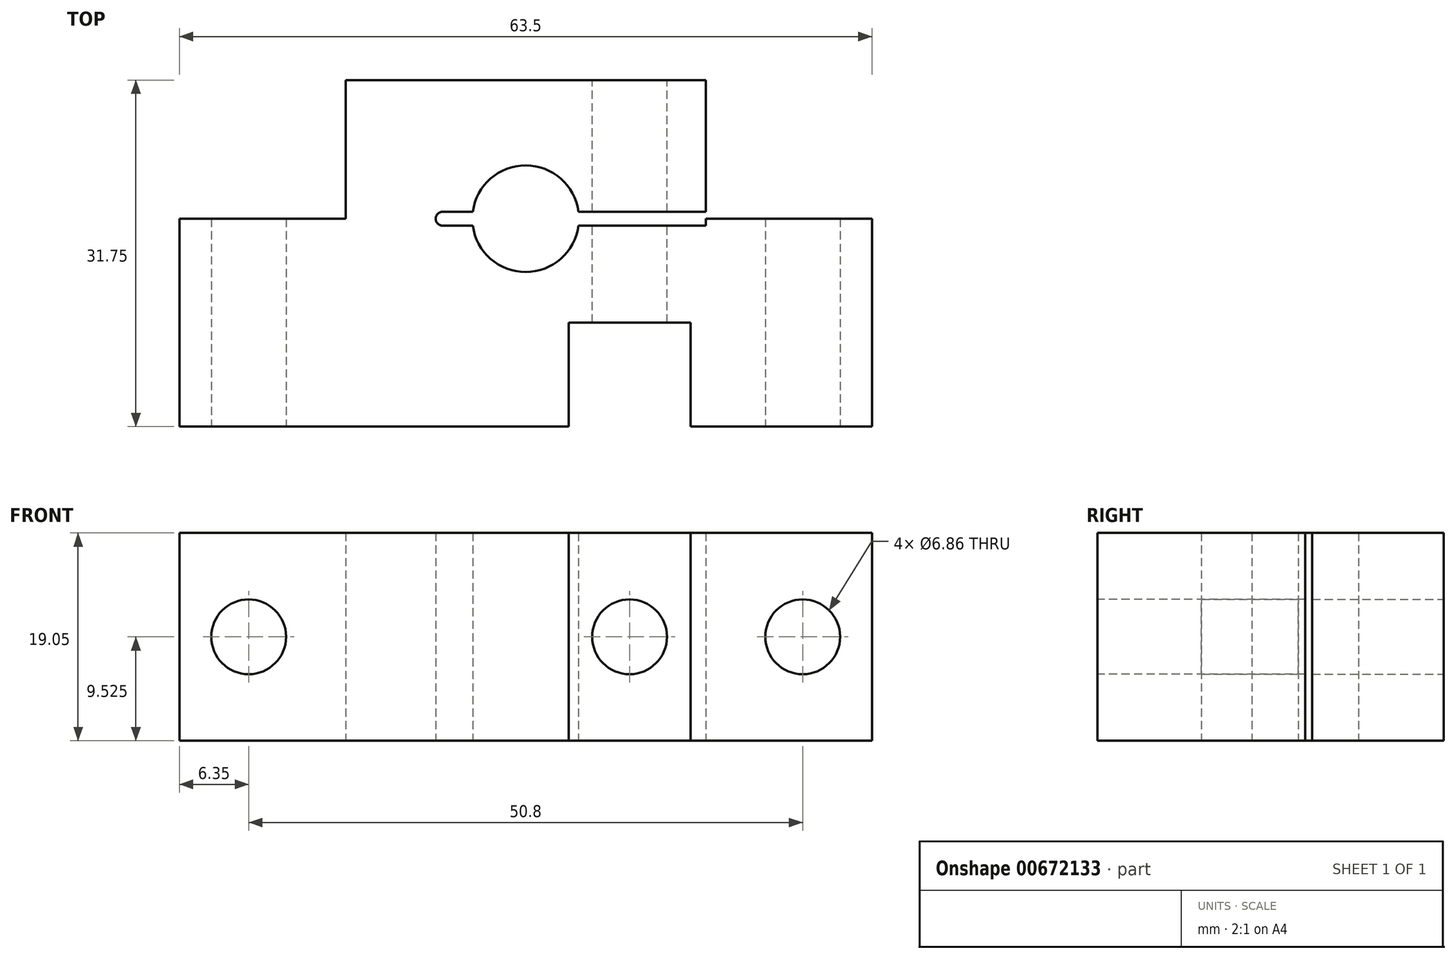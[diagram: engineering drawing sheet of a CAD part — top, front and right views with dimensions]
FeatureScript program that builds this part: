
annotation { "Feature Type Name" : "Feature", "Feature Type Description" : "" }
export const myFeature = defineFeature(function(context is Context, id is Id, definition is map)
    precondition{}
    {
        {
            var Q0;
            Q0=qCreatedBy(makeId("Top.planeOp"),FACE);
            var sketch = newSketch(context, id + "F0", { "sketchPlane" : qUnion([Q0])});
            skLineSegment(sketch, "E0.bottom", {"start": v(-31.75, 0) * mm, "end": v(31.75, 0) * mm});
            skLineSegment(sketch, "E0.top", {"start": v(-16.51, 31.75) * mm, "end": v(16.51, 31.75) * mm});
            skLineSegment(sketch, "E0.left", {"start": v(-31.75, 0) * mm, "end": v(-31.75, 19.05) * mm});
            skLineSegment(sketch, "E0.right", {"start": v(31.75, 0) * mm, "end": v(31.75, 19.05) * mm});
            skLineSegment(sketch, "E1", {"start": v(31.75, 19.05) * mm, "end": v(16.51, 19.05) * mm});
            skLineSegment(sketch, "E2", {"start": v(16.51, 19.05) * mm, "end": v(16.51, 31.75) * mm});
            skLineSegment(sketch, "E3", {"start": v(-31.75, 19.05) * mm, "end": v(-16.51, 19.05) * mm});
            skLineSegment(sketch, "E4", {"start": v(-16.51, 19.05) * mm, "end": v(-16.51, 31.75) * mm});
            skSolve(sketch);
        }
        {
            var Q0;
            Q0 = qSketchRegion(id + "F0", true);
            extrude(context, id + "F1", {"entities" : qUnion([Q0]), "depth" : 19.05 * mm, "offsetDistance" : 25.4 * mm});
        }
        {
            var Q0;
            Q0=qCreatedBy(makeId("Top.planeOp"),FACE);
            var sketch = newSketch(context, id + "F2", { "sketchPlane" : qUnion([Q0])});
            skArc(sketch, "E5", {"start": v(-4.85, 18.41) * mm, "mid": v(0, 14.16) * mm, "end": v(4.85, 18.41) * mm});
            skLineSegment(sketch, "E6.0", {"start": v(16.51, 18.42) * mm, "end": v(16.51, 19.69) * mm});
            skLineSegment(sketch, "E7", {"start": v(4.85, 19.68) * mm, "end": v(16.51, 19.68) * mm});
            skLineSegment(sketch, "E8", {"start": v(16.51, 19.69) * mm, "end": v(16.51, 18.42) * mm});
            skLineSegment(sketch, "E9", {"start": v(16.51, 18.42) * mm, "end": v(4.85, 18.41) * mm});
            skLineSegment(sketch, "E10", {"start": v(-7.62, 19.68) * mm, "end": v(-4.85, 19.68) * mm});
            skPoint(sketch, "E11.orphan", {"position": v(0, 19.68) * mm});
            skLineSegment(sketch, "E12.trimOffspring", {"start": v(-4.85, 18.41) * mm, "end": v(-7.62, 18.41) * mm});
            skArc(sketch, "E13.trimOffspring", {"start": v(4.85, 19.68) * mm, "mid": v(0, 23.94) * mm, "end": v(-4.85, 19.68) * mm});
            skArc(sketch, "E14", {"start": v(-7.62, 19.69) * mm, "mid": v(-8.26, 19.05) * mm, "end": v(-7.62, 18.41) * mm});
            skPoint(sketch, "E15.orphan", {"position": v(16.51, 31.75) * mm});
            skPoint(sketch, "E16.orphan", {"position": v(16.51, 19.05) * mm});
            skSolve(sketch);
        }
        {
            var Q0;
            Q0 = qSketchRegion(id + "F2", true);
            extrude(context, id + "F3", {"entities" : qUnion([Q0]), "operationType" : NewBodyOperationType.REMOVE, "endBound" : BoundingType.THROUGH_ALL, "depth" : 25.4 * mm, "offsetDistance" : 25.4 * mm});
        }
        {
            var Q0;
            Q0=qCreatedBy(makeId("Front.planeOp"),FACE);
            var sketch = newSketch(context, id + "F4", { "sketchPlane" : qUnion([Q0])});
            skCircle(sketch, "E17", {"center": v(25.4, 9.53) * mm, "radius": 3.43 * mm});
            skCircle(sketch, "E18", {"center": v(-25.4, 9.53) * mm, "radius": 3.43 * mm});
            skSolve(sketch);
        }
        {
            var Q0;
            Q0 = qSketchRegion(id + "F4", true);
            extrude(context, id + "F5", {"entities" : qUnion([Q0]), "operationType" : NewBodyOperationType.REMOVE, "endBound" : BoundingType.THROUGH_ALL, "oppositeDirection" : true, "depth" : 25.4 * mm, "offsetDistance" : 25.4 * mm});
        }
        {
            var Q0;
            Q0=qCreatedBy(makeId("Front.planeOp"),FACE);
            var sketch = newSketch(context, id + "F6", { "sketchPlane" : qUnion([Q0])});
            skLineSegment(sketch, "E19.0", {"start": v(3.94, 19.05) * mm, "end": v(15.11, 19.05) * mm});
            skLineSegment(sketch, "E20.0", {"start": v(3.94, 0) * mm, "end": v(15.11, 0) * mm});
            skLineSegment(sketch, "E21", {"start": v(3.94, 19.05) * mm, "end": v(3.94, 0) * mm});
            skLineSegment(sketch, "E22", {"start": v(15.11, 19.05) * mm, "end": v(15.11, 0) * mm});
            skPoint(sketch, "E23.orphan", {"position": v(31.75, 19.05) * mm});
            skPoint(sketch, "E24.orphan", {"position": v(31.75, 0) * mm});
            skPoint(sketch, "E25.orphan", {"position": v(-31.75, 0) * mm});
            skPoint(sketch, "E26.orphan", {"position": v(-31.75, 19.05) * mm});
            skSolve(sketch);
        }
        {
            var Q0;
            Q0 = qSketchRegion(id + "F6", true);
            extrude(context, id + "F7", {"entities" : qUnion([Q0]), "operationType" : NewBodyOperationType.REMOVE, "oppositeDirection" : true, "depth" : 9.52 * mm, "offsetDistance" : 25.4 * mm});
        }
        {
            var Q0;
            Q0=makeQuery(id+"F1.opExtrude","SWEPT_FACE",FACE,{"disambiguationData":[OSD([sQuery(id+"F0.wireOp",EDGE,"E0.top")])]});
            var sketch = newSketch(context, id + "F8", { "sketchPlane" : qUnion([Q0])});
            skCircle(sketch, "E27", {"center": v(-9.53, 9.52) * mm, "radius": 3.43 * mm});
            skSolve(sketch);
        }
        {
            var Q0;
            Q0 = qSketchRegion(id + "F8", true);
            extrude(context, id + "F9", {"entities" : qUnion([Q0]), "operationType" : NewBodyOperationType.REMOVE, "endBound" : BoundingType.THROUGH_ALL, "oppositeDirection" : true, "depth" : 25.4 * mm, "offsetDistance" : 25.4 * mm});
        }
    });
